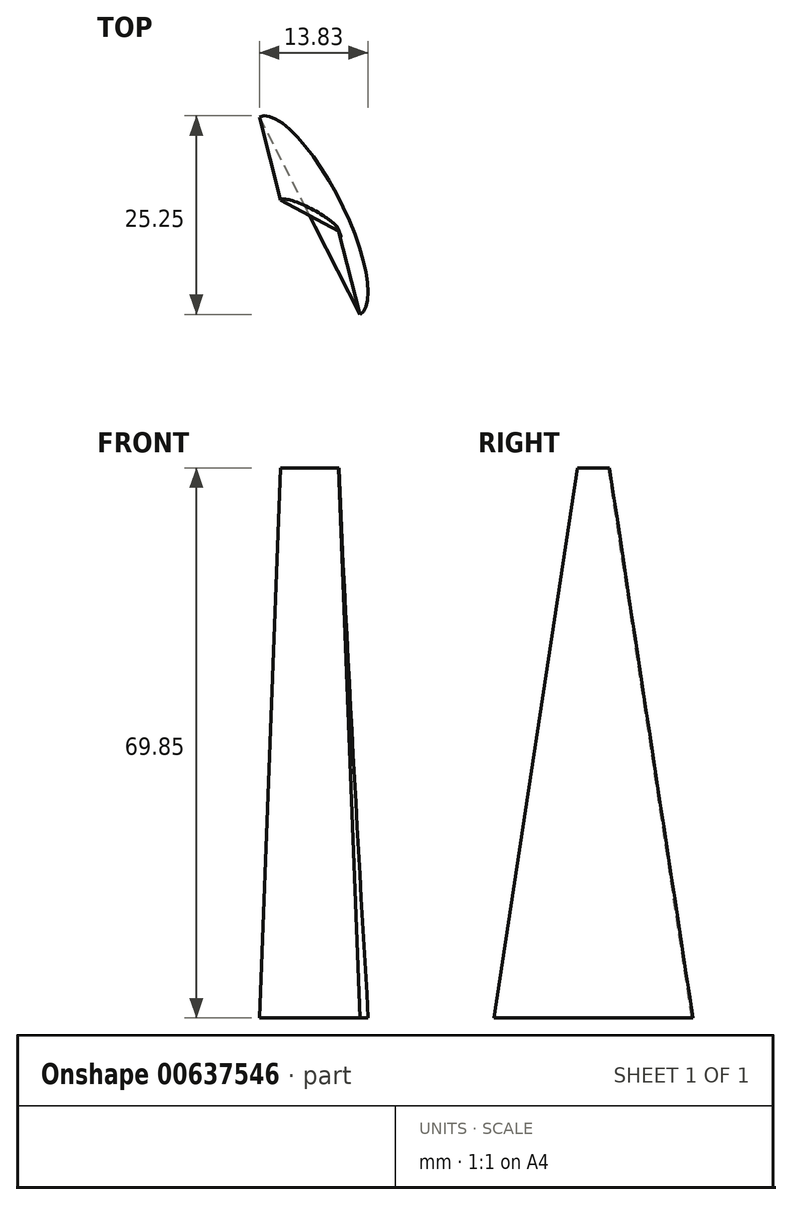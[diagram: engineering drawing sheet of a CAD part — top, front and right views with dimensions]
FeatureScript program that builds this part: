
annotation { "Feature Type Name" : "Feature", "Feature Type Description" : "" }
export const myFeature = defineFeature(function(context is Context, id is Id, definition is map)
    precondition{}
    {
        {
            var Q0;
            Q0=qCreatedBy(makeId("Top.planeOp"),FACE);
            cPlane(context, id + "F0", {"entities" : qUnion([Q0]), "cplaneType" : CPlaneType.OFFSET, "offset" : 6.35 * mm, "width" : 152.4 * mm, "height" : 152.4 * mm});
        }
        {
            var Q0;
            Q0=qCreatedBy(id+"F0.planeOp",FACE);
            cPlane(context, id + "F1", {"entities" : qUnion([Q0]), "cplaneType" : CPlaneType.OFFSET, "offset" : 6.35 * mm, "width" : 152.4 * mm, "height" : 152.4 * mm});
        }
        {
            var Q0;
            Q0=qCreatedBy(id+"F1.planeOp",FACE);
            cPlane(context, id + "F2", {"entities" : qUnion([Q0]), "cplaneType" : CPlaneType.OFFSET, "offset" : 6.35 * mm, "width" : 152.4 * mm, "height" : 152.4 * mm});
        }
        {
            var Q0;
            Q0=qCreatedBy(id+"F2.planeOp",FACE);
            cPlane(context, id + "F3", {"entities" : qUnion([Q0]), "cplaneType" : CPlaneType.OFFSET, "offset" : 6.35 * mm, "width" : 152.4 * mm, "height" : 152.4 * mm});
        }
        {
            var Q0;
            Q0=qCreatedBy(id+"F3.planeOp",FACE);
            cPlane(context, id + "F4", {"entities" : qUnion([Q0]), "cplaneType" : CPlaneType.OFFSET, "offset" : 6.35 * mm, "width" : 152.4 * mm, "height" : 152.4 * mm});
        }
        {
            var Q0;
            Q0=qCreatedBy(id+"F4.planeOp",FACE);
            cPlane(context, id + "F5", {"entities" : qUnion([Q0]), "cplaneType" : CPlaneType.OFFSET, "offset" : 6.35 * mm, "width" : 152.4 * mm, "height" : 152.4 * mm});
        }
        {
            var Q0;
            Q0=qCreatedBy(id+"F5.planeOp",FACE);
            cPlane(context, id + "F6", {"entities" : qUnion([Q0]), "cplaneType" : CPlaneType.OFFSET, "offset" : 6.35 * mm, "width" : 152.4 * mm, "height" : 152.4 * mm});
        }
        {
            var Q0;
            Q0=qCreatedBy(id+"F6.planeOp",FACE);
            cPlane(context, id + "F7", {"entities" : qUnion([Q0]), "cplaneType" : CPlaneType.OFFSET, "offset" : 6.35 * mm, "width" : 152.4 * mm, "height" : 152.4 * mm});
        }
        {
            var Q0;
            Q0=qCreatedBy(id+"F7.planeOp",FACE);
            cPlane(context, id + "F8", {"entities" : qUnion([Q0]), "cplaneType" : CPlaneType.OFFSET, "offset" : 6.35 * mm, "width" : 152.4 * mm, "height" : 152.4 * mm});
        }
        {
            var Q0;
            Q0=qCreatedBy(id+"F8.planeOp",FACE);
            cPlane(context, id + "F9", {"entities" : qUnion([Q0]), "cplaneType" : CPlaneType.OFFSET, "offset" : 6.35 * mm, "width" : 152.4 * mm, "height" : 152.4 * mm});
        }
        {
            var Q0;
            Q0=qCreatedBy(id+"F9.planeOp",FACE);
            cPlane(context, id + "F10", {"entities" : qUnion([Q0]), "cplaneType" : CPlaneType.OFFSET, "offset" : 6.35 * mm, "width" : 152.4 * mm, "height" : 152.4 * mm});
        }
        {
            var Q0;
            Q0=qCreatedBy(id+"F10.planeOp",FACE);
            cPlane(context, id + "F11", {"entities" : qUnion([Q0]), "cplaneType" : CPlaneType.OFFSET, "offset" : 6.35 * mm, "width" : 152.4 * mm, "height" : 152.4 * mm});
        }
        {
            var Q0;
            Q0=qCreatedBy(makeId("Right.planeOp"),FACE);
            var sketch = newSketch(context, id + "F12", { "sketchPlane" : qUnion([Q0])});
            skLineSegment(sketch, "E0", {"start": v(12.7, 6.35) * mm, "end": v(-12.7, 6.35) * mm});
            skPoint(sketch, "E1", {"position": v(0, 6.35) * mm});
            skLineSegment(sketch, "E2", {"start": v(2.12, 76.2) * mm, "end": v(-2.12, 76.2) * mm});
            skPoint(sketch, "E3", {"position": v(0, 76.2) * mm});
            skLineSegment(sketch, "E4", {"start": v(-2.12, 76.2) * mm, "end": v(-12.7, 6.35) * mm});
            skLineSegment(sketch, "E5", {"start": v(2.12, 76.2) * mm, "end": v(12.7, 6.35) * mm});
            skPoint(sketch, "E6", {"position": v(11.74, 12.7) * mm});
            skPoint(sketch, "E7", {"position": v(10.78, 19.05) * mm});
            skPoint(sketch, "E8", {"position": v(9.81, 25.4) * mm});
            skPoint(sketch, "E9", {"position": v(8.85, 31.75) * mm});
            skPoint(sketch, "E10", {"position": v(7.89, 38.1) * mm});
            skPoint(sketch, "E11", {"position": v(6.93, 44.45) * mm});
            skPoint(sketch, "E12", {"position": v(5.97, 50.8) * mm});
            skPoint(sketch, "E13", {"position": v(5, 57.15) * mm});
            skPoint(sketch, "E14", {"position": v(4.04, 63.5) * mm});
            skPoint(sketch, "E15", {"position": v(3.08, 69.85) * mm});
            skSolve(sketch);
        }
        {
            var Q0;
            Q0=qCreatedBy(makeId("Top.planeOp"),FACE);
            var sketch = newSketch(context, id + "F13", { "sketchPlane" : qUnion([Q0])});
            skPoint(sketch, "E16.0", {"position": v(0, 12.7) * mm});
            skPoint(sketch, "E17.0", {"position": v(0, -12.7) * mm});
            skLineSegment(sketch, "E18", {"start": v(-51.06, 12.7) * mm, "end": v(60.83, 12.7) * mm});
            skLineSegment(sketch, "E19", {"start": v(-49.79, -12.7) * mm, "end": v(63.01, -12.7) * mm});
            skPoint(sketch, "E20.0", {"position": v(0, 11.74) * mm});
            skPoint(sketch, "E21.0", {"position": v(0, 10.78) * mm});
            skPoint(sketch, "E22.0", {"position": v(0, 9.81) * mm});
            skPoint(sketch, "E23.0", {"position": v(0, 8.85) * mm});
            skPoint(sketch, "E24.0", {"position": v(0, 7.89) * mm});
            skPoint(sketch, "E25.0", {"position": v(0, 6.93) * mm});
            skPoint(sketch, "E26.0", {"position": v(0, 5.97) * mm});
            skPoint(sketch, "E27.0", {"position": v(0, 5) * mm});
            skPoint(sketch, "E28.0", {"position": v(0, 4.04) * mm});
            skPoint(sketch, "E29.0", {"position": v(0, 3.08) * mm});
            skPoint(sketch, "E30.0", {"position": v(0, 2.12) * mm});
            skLineSegment(sketch, "E31", {"start": v(0, 11.74) * mm, "end": v(-28.18, 11.74) * mm});
            skLineSegment(sketch, "E32", {"start": v(0, 10.78) * mm, "end": v(-29.4, 10.78) * mm});
            skLineSegment(sketch, "E33", {"start": v(0, 9.81) * mm, "end": v(-30.69, 9.81) * mm});
            skLineSegment(sketch, "E34", {"start": v(0, 8.85) * mm, "end": v(-32.79, 8.85) * mm});
            skLineSegment(sketch, "E35", {"start": v(0, 7.89) * mm, "end": v(-33.76, 7.89) * mm});
            skLineSegment(sketch, "E36", {"start": v(0, 6.93) * mm, "end": v(-35.38, 6.93) * mm});
            skLineSegment(sketch, "E37", {"start": v(0, 5.97) * mm, "end": v(-40.56, 5.97) * mm});
            skLineSegment(sketch, "E38", {"start": v(0, 5) * mm, "end": v(-43.8, 5) * mm});
            skLineSegment(sketch, "E39", {"start": v(0, 4.04) * mm, "end": v(-44.84, 4.04) * mm});
            skLineSegment(sketch, "E40", {"start": v(0, 3.08) * mm, "end": v(-48.8, 3.08) * mm});
            skLineSegment(sketch, "E41", {"start": v(0, 2.12) * mm, "end": v(-50.1, 2.12) * mm});
            skPoint(sketch, "E42", {"position": v(0, 13.66) * mm});
            skLineSegment(sketch, "E43", {"start": v(0, 13.66) * mm, "end": v(-11.96, 13.66) * mm});
            skSolve(sketch);
        }
        {
            var Q0;
            Q0=qCreatedBy(id+"F0.planeOp",FACE);
            var sketch = newSketch(context, id + "F14", { "sketchPlane" : qUnion([Q0])});
            skLineSegment(sketch, "E44.0", {"start": v(-51.06, 12.7) * mm, "end": v(60.83, 12.7) * mm});
            skEllipse(sketch, "E45", {"center": v(0, 0) * mm, "majorRadius": 14.08 * mm, "minorRadius": 4.3 * mm, "majorAxis": v(-0.45, 0.9)});
            skLineSegment(sketch, "E46", {"start": v(-6.38, 12.55) * mm, "end": v(6.38, -12.55) * mm});
            skSolve(sketch);
        }
        {
            var Q0;
            Q0=qCreatedBy(id+"F11.planeOp",FACE);
            var sketch = newSketch(context, id + "F15", { "sketchPlane" : qUnion([Q0])});
            skLineSegment(sketch, "E47.0", {"start": v(0, 2.12) * mm, "end": v(-50.1, 2.12) * mm});
            skEllipse(sketch, "E48", {"center": v(0, 0) * mm, "majorRadius": 4.18 * mm, "minorRadius": 0.89 * mm, "majorAxis": v(-0.88, 0.47)});
            skLineSegment(sketch, "E49", {"start": v(-3.7, 1.97) * mm, "end": v(3.7, -1.97) * mm});
            skSolve(sketch);
        }
        {
            var Q0;
            Q0=makeQuery(id+"F14.imprint","IMPRINT",FACE,{"disambiguationData":[TD([[makeQuery(id+"F14.imprint","IMPRINT",EDGE,{"derivedFrom":sQuery(id+"F14.wireOp",EDGE,"E45")}),1.0]])]});
            var Q1;
            Q1=makeQuery(id+"F15.imprint","IMPRINT",FACE,{"disambiguationData":[TD([[makeQuery(id+"F15.imprint","IMPRINT",EDGE,{"derivedFrom":sQuery(id+"F15.wireOp",EDGE,"E48")}),1.0]])]});
            loft(context, id + "F16", {"sheetProfilesArray" : [{ "sheetProfileEntities" : qUnion([Q0]) }, { "sheetProfileEntities" : qUnion([Q1]) }]});
        }
        {
            var Q0;
            Q0=makeQuery(id+"F16.opLoft","CAP_FACE",FACE,{"disambiguationData":[OSD([makeQuery(id+"F14.imprint","IMPRINT",FACE,{"disambiguationData":[TD([[makeQuery(id+"F14.imprint","IMPRINT",EDGE,{"derivedFrom":sQuery(id+"F14.wireOp",EDGE,"E45")}),1.0]])]})])],"isStart":true});
            var sketch = newSketch(context, id + "F17", { "sketchPlane" : qUnion([Q0])});
            skCircle(sketch, "E50", {"center": v(0, 0) * mm, "radius": 1.52 * mm});
            skSolve(sketch);
        }
        {
            var Q0;
            Q0 = qSketchRegion(id + "F17", true);
            extrude(context, id + "F18", {"entities" : qUnion([Q0]), "operationType" : NewBodyOperationType.REMOVE, "oppositeDirection" : true, "depth" : 1 / 101.6 * mm, "offsetDistance" : 25.4 * mm});
        }
    });
